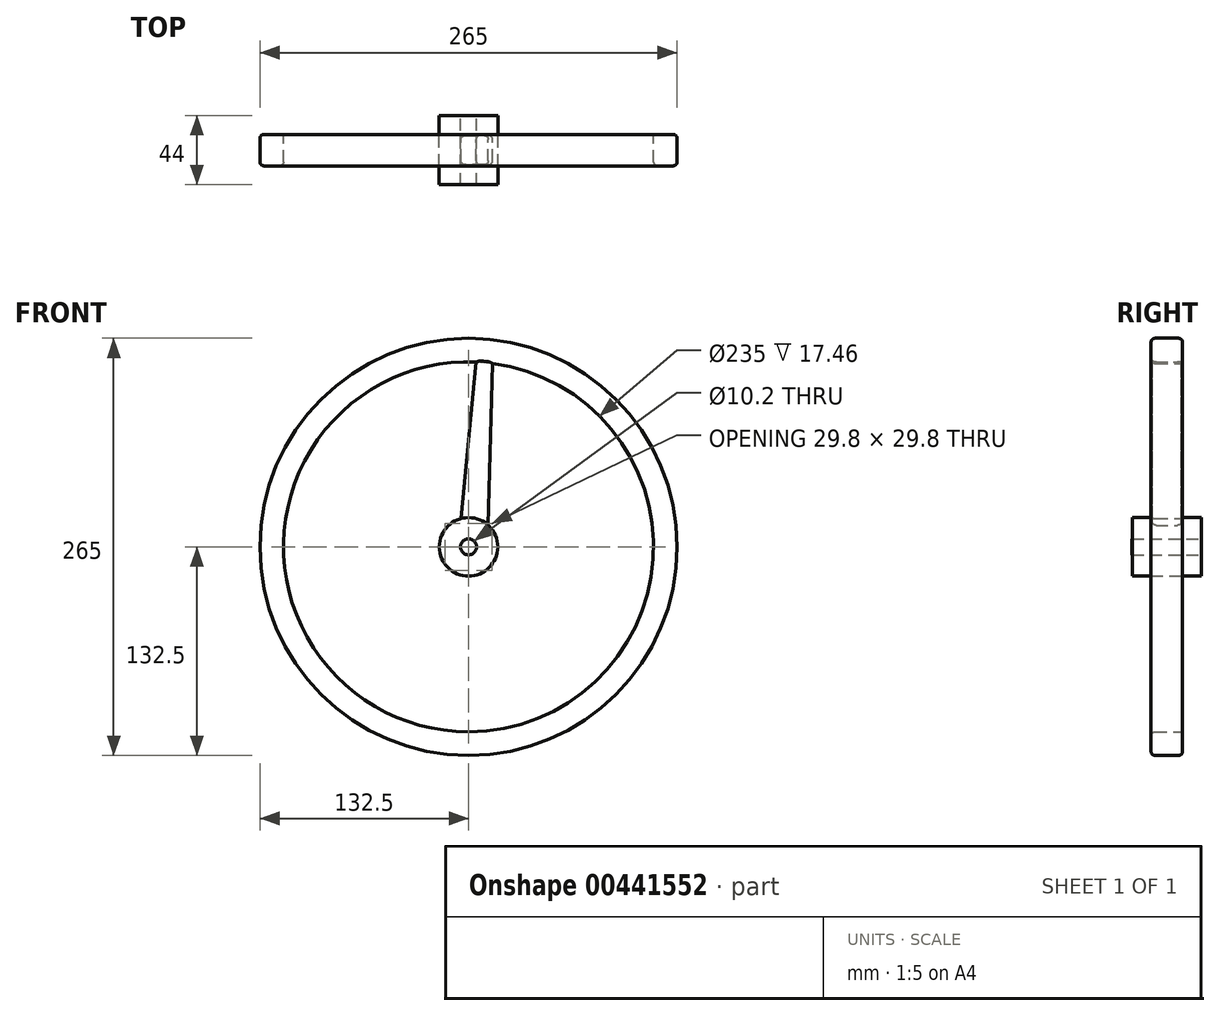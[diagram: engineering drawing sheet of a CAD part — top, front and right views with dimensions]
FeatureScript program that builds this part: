
annotation { "Feature Type Name" : "Feature", "Feature Type Description" : "" }
export const myFeature = defineFeature(function(context is Context, id is Id, definition is map)
    precondition{}
    {
        {
            var Q0;
            Q0=qCreatedBy(makeId("Front.planeOp"),FACE);
            var sketch = newSketch(context, id + "F0", { "sketchPlane" : qUnion([Q0])});
            skCircle(sketch, "E0", {"center": v(0, 0) * mm, "radius": 132.5 * mm});
            skCircle(sketch, "E1", {"center": v(0, 0) * mm, "radius": 117.5 * mm});
            skCircle(sketch, "E2", {"center": v(0, 0) * mm, "radius": 14.9 * mm});
            skCircle(sketch, "E3", {"center": v(0, 0) * mm, "radius": 5.1 * mm});
            skCircle(sketch, "E4", {"center": v(0, 0) * mm, "radius": 18.58 * mm});
            skSolve(sketch);
        }
        {
            var Q0;
            Q0=makeQuery(id+"F0.imprint","IMPRINT",FACE,{"disambiguationData":[TD([[makeQuery(id+"F0.imprint","IMPRINT",EDGE,{"derivedFrom":sQuery(id+"F0.wireOp",EDGE,"E0")}),1.0]])]});
            var Q1;
            Q1=makeQuery(id+"F0.imprint","IMPRINT",FACE,{"disambiguationData":[TD([[makeQuery(id+"F0.imprint","IMPRINT",EDGE,{"derivedFrom":sQuery(id+"F0.wireOp",EDGE,"nvnF9JJx-96JA-hIOM-i3RK-gnpj2jDfy9Uj")}),1.0]])]});
            var Q2;
            Q2=makeQuery(id+"F0.imprint","IMPRINT",FACE,{"disambiguationData":[TD([[makeQuery(id+"F0.imprint","IMPRINT",EDGE,{"derivedFrom":sQuery(id+"F0.wireOp",EDGE,"E2")}),1.0]])]});
            extrude(context, id + "F1", {"entities" : qUnion([Q0, Q1, Q2]), "endBound" : BoundingType.SYMMETRIC, "depth" : 20 * mm});
        }
        {
            var Q0;
            Q0=makeQuery(id+"F0.imprint","IMPRINT",FACE,{"disambiguationData":[TD([[makeQuery(id+"F0.imprint","IMPRINT",EDGE,{"derivedFrom":sQuery(id+"F0.wireOp",EDGE,"E2")}),-1.0]])]});
            extrude(context, id + "F2", {"entities" : qUnion([Q0]), "endBound" : BoundingType.SYMMETRIC, "depth" : 19.99 * mm});
        }
        {
            var Q0;
            Q0=makeQuery(id+"F0.imprint","IMPRINT",FACE,{"disambiguationData":[TD([[makeQuery(id+"F0.imprint","IMPRINT",EDGE,{"derivedFrom":sQuery(id+"F0.wireOp",EDGE,"E1")}),1.0]])]});
            var sketch = newSketch(context, id + "F3", { "sketchPlane" : qUnion([Q0])});
            skArc(sketch, "E5.0", {"start": v(12.52, 13.72) * mm, "mid": v(4.35, 18.06) * mm, "end": v(-4.9, 17.92) * mm});
            skArc(sketch, "E6.0", {"start": v(15.3, 116.5) * mm, "mid": v(10.06, 117.07) * mm, "end": v(4.8, 117.4) * mm});
            skLineSegment(sketch, "E7", {"start": v(-4.9, 17.92) * mm, "end": v(4.8, 117.4) * mm});
            skLineSegment(sketch, "E8", {"start": v(12.52, 13.72) * mm, "end": v(15.3, 116.5) * mm});
            skSolve(sketch);
        }
        {
            var Q0;
            Q0=makeQuery(id+"F3.imprint","IMPRINT",FACE,{"disambiguationData":[TD([[makeQuery(id+"F3.imprint","IMPRINT",EDGE,{"derivedFrom":sQuery(id+"F3.wireOp",EDGE,"E5.0")}),-1.0]])]});
            extrude(context, id + "F4", {"entities" : qUnion([Q0]), "operationType" : NewBodyOperationType.ADD, "endBound" : BoundingType.SYMMETRIC, "depth" : 18.54 * mm});
        }
        {
            var Q0;
            Q0=makeQuery(id+"F2.opExtrude","CAP_FACE",FACE,{"disambiguationData":[OSD([sQuery(id+"F0.wireOp",EDGE,"E2"),sQuery(id+"F0.wireOp",EDGE,"E4")])],"isStart":false});
            var Q1;
            Q1=makeQuery(id+"F1.opExtrude","CAP_FACE",FACE,{"disambiguationData":[OSD([sQuery(id+"F0.wireOp",EDGE,"E2"),sQuery(id+"F0.wireOp",EDGE,"E3")])],"isStart":false});
            extrude(context, id + "F5", {"entities" : qUnion([Q0, Q1]), "operationType" : NewBodyOperationType.ADD, "depth" : 12 * mm});
        }
        {
            var Q0;
            Q0=makeQuery(id+"F1.opExtrude","CAP_FACE",FACE,{"disambiguationData":[OSD([sQuery(id+"F0.wireOp",EDGE,"E2"),sQuery(id+"F0.wireOp",EDGE,"E3")])],"isStart":true});
            var Q1;
            Q1=makeQuery(id+"F2.opExtrude","CAP_FACE",FACE,{"disambiguationData":[OSD([sQuery(id+"F0.wireOp",EDGE,"E2"),sQuery(id+"F0.wireOp",EDGE,"E4")])],"isStart":true});
            extrude(context, id + "F6", {"entities" : qUnion([Q0, Q1]), "operationType" : NewBodyOperationType.ADD, "depth" : 12 * mm});
        }
        {
            var Q0;
            Q0=makeQuery(id+"F1.opExtrude","SWEPT_FACE",FACE,{"disambiguationData":[OSD([sQuery(id+"F0.wireOp",EDGE,"E0")])]});
            var Q1;
            Q1=makeQuery(id+"F1.opExtrude","CAP_FACE",FACE,{"disambiguationData":[OSD([sQuery(id+"F0.wireOp",EDGE,"E0"),sQuery(id+"F0.wireOp",EDGE,"E1")])],"isStart":false});
            fillet(context, id + "F7", {"entities" : qUnion([Q0, Q1]), "radius" : 2.54 * mm, "tangentPropagation" : true, "allowEdgeOverflow" : false});
        }
        {
            var Q0;
            Q0=makeQuery(id+"F4.opExtrude","CAP_EDGE",EDGE,{"disambiguationData":[OSD([sQuery(id+"F3.wireOp",EDGE,"E8")])],"isStart":false});
            var Q1;
            Q1=makeQuery(id+"F4.opExtrude","CAP_EDGE",EDGE,{"disambiguationData":[OSD([sQuery(id+"F3.wireOp",EDGE,"E8")])],"isStart":true});
            var Q2;
            Q2=makeQuery(id+"F4.opExtrude","CAP_EDGE",EDGE,{"disambiguationData":[OSD([sQuery(id+"F3.wireOp",EDGE,"E7")])],"isStart":true});
            var Q3;
            Q3=makeQuery(id+"F4.opExtrude","CAP_EDGE",EDGE,{"disambiguationData":[OSD([sQuery(id+"F3.wireOp",EDGE,"E7")])],"isStart":false});
            var Q4;
            Q4=makeQuery(id+"Fbn3vmABT5rwXxv_3.1.F4.opExtrude","CAP_EDGE",EDGE,{"disambiguationData":[OSD([sQuery(id+"F3.wireOp",EDGE,"E8")])],"isStart":true});
            var Q5;
            Q5=makeQuery(id+"Fbn3vmABT5rwXxv_3.1.F4.opExtrude","CAP_EDGE",EDGE,{"disambiguationData":[OSD([sQuery(id+"F3.wireOp",EDGE,"E8")])],"isStart":false});
            var Q6;
            Q6=makeQuery(id+"Fbn3vmABT5rwXxv_3.1.F4.opExtrude","CAP_EDGE",EDGE,{"disambiguationData":[OSD([sQuery(id+"F3.wireOp",EDGE,"E7")])],"isStart":false});
            var Q7;
            Q7=makeQuery(id+"Fbn3vmABT5rwXxv_3.1.F4.opExtrude","CAP_EDGE",EDGE,{"disambiguationData":[OSD([sQuery(id+"F3.wireOp",EDGE,"E7")])],"isStart":true});
            var Q8;
            Q8=makeQuery(id+"Fbn3vmABT5rwXxv_3.2.F4.opExtrude","CAP_EDGE",EDGE,{"disambiguationData":[OSD([sQuery(id+"F3.wireOp",EDGE,"E8")])],"isStart":true});
            var Q9;
            Q9=makeQuery(id+"Fbn3vmABT5rwXxv_3.2.F4.opExtrude","CAP_EDGE",EDGE,{"disambiguationData":[OSD([sQuery(id+"F3.wireOp",EDGE,"E7")])],"isStart":true});
            var Q10;
            Q10=makeQuery(id+"Fbn3vmABT5rwXxv_3.2.F4.opExtrude","CAP_EDGE",EDGE,{"disambiguationData":[OSD([sQuery(id+"F3.wireOp",EDGE,"E8")])],"isStart":false});
            var Q11;
            Q11=makeQuery(id+"Fbn3vmABT5rwXxv_3.2.F4.opExtrude","CAP_EDGE",EDGE,{"disambiguationData":[OSD([sQuery(id+"F3.wireOp",EDGE,"E7")])],"isStart":false});
            var Q12;
            Q12=makeQuery(id+"Fbn3vmABT5rwXxv_3.3.F4.opExtrude","CAP_EDGE",EDGE,{"disambiguationData":[OSD([sQuery(id+"F3.wireOp",EDGE,"E8")])],"isStart":false});
            var Q13;
            Q13=makeQuery(id+"Fbn3vmABT5rwXxv_3.3.F4.opExtrude","CAP_EDGE",EDGE,{"disambiguationData":[OSD([sQuery(id+"F3.wireOp",EDGE,"E7")])],"isStart":false});
            var Q14;
            Q14=makeQuery(id+"Fbn3vmABT5rwXxv_3.4.F4.opExtrude","CAP_EDGE",EDGE,{"disambiguationData":[OSD([sQuery(id+"F3.wireOp",EDGE,"E8")])],"isStart":false});
            var Q15;
            Q15=makeQuery(id+"Fbn3vmABT5rwXxv_3.4.F4.opExtrude","CAP_EDGE",EDGE,{"disambiguationData":[OSD([sQuery(id+"F3.wireOp",EDGE,"E7")])],"isStart":false});
            var Q16;
            Q16=makeQuery(id+"Fbn3vmABT5rwXxv_3.5.F4.opExtrude","CAP_EDGE",EDGE,{"disambiguationData":[OSD([sQuery(id+"F3.wireOp",EDGE,"E8")])],"isStart":false});
            var Q17;
            Q17=makeQuery(id+"Fbn3vmABT5rwXxv_3.5.F4.opExtrude","CAP_EDGE",EDGE,{"disambiguationData":[OSD([sQuery(id+"F3.wireOp",EDGE,"E7")])],"isStart":false});
            var Q18;
            Q18=makeQuery(id+"Fbn3vmABT5rwXxv_3.3.F4.opExtrude","CAP_EDGE",EDGE,{"disambiguationData":[OSD([sQuery(id+"F3.wireOp",EDGE,"E8")])],"isStart":true});
            var Q19;
            Q19=makeQuery(id+"Fbn3vmABT5rwXxv_3.3.F4.opExtrude","CAP_EDGE",EDGE,{"disambiguationData":[OSD([sQuery(id+"F3.wireOp",EDGE,"E7")])],"isStart":true});
            var Q20;
            Q20=makeQuery(id+"Fbn3vmABT5rwXxv_3.4.F4.opExtrude","CAP_EDGE",EDGE,{"disambiguationData":[OSD([sQuery(id+"F3.wireOp",EDGE,"E8")])],"isStart":true});
            var Q21;
            Q21=makeQuery(id+"Fbn3vmABT5rwXxv_3.4.F4.opExtrude","CAP_EDGE",EDGE,{"disambiguationData":[OSD([sQuery(id+"F3.wireOp",EDGE,"E7")])],"isStart":true});
            var Q22;
            Q22=makeQuery(id+"Fbn3vmABT5rwXxv_3.5.F4.opExtrude","CAP_EDGE",EDGE,{"disambiguationData":[OSD([sQuery(id+"F3.wireOp",EDGE,"E8")])],"isStart":true});
            var Q23;
            Q23=makeQuery(id+"Fbn3vmABT5rwXxv_3.5.F4.opExtrude","CAP_EDGE",EDGE,{"disambiguationData":[OSD([sQuery(id+"F3.wireOp",EDGE,"E7")])],"isStart":true});
            fillet(context, id + "F8", {"entities" : qUnion([Q0, Q1, Q2, Q3, Q4, Q5, Q6, Q7, Q8, Q9, Q10, Q11, Q12, Q13, Q14, Q15, Q16, Q17, Q18, Q19, Q20, Q21, Q22, Q23]), "radius" : 2.54 * mm, "tangentPropagation" : true, "allowEdgeOverflow" : false});
        }
    });
